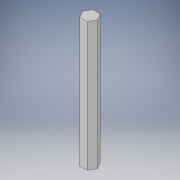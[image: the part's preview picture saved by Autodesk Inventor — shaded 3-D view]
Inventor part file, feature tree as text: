
AUTODESK INVENTOR PART (.ipt)
format: ipt  version: 2019 (Build 230136000, 136)  size: 96,768 bytes
history: native  units: in
note: dims shown in document units (in); Inventor stores cm internally (conversion verified against a paired STEP export)
features: extrude x1, sketch x1
ambient origin geometry x8: Origin, YZ Plane, XZ Plane, XY Plane, X Axis, Y Axis, Z Axis, Center Point
bodies: Solid1 (feature_tree)
feature tree (2):
  extrude  "Extrusion1"  Depth=0.29in
  sketch  "Sketch1"  dims[d1=5.0in d2=0.0in d3=0.29in]
